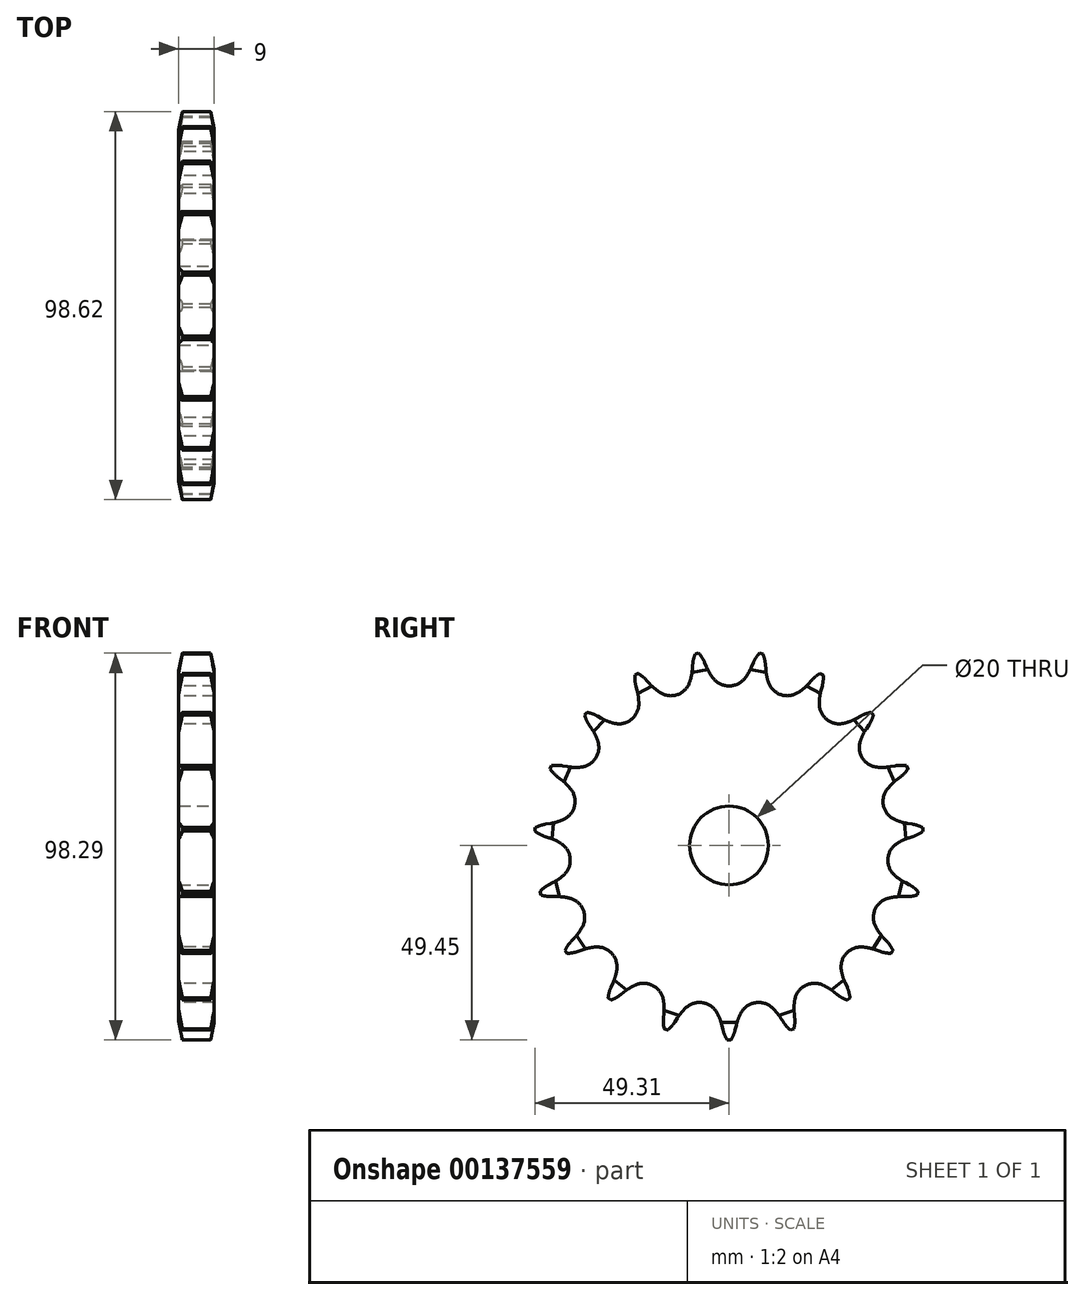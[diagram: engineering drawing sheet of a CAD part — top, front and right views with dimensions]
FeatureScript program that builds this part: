
annotation { "Feature Type Name" : "Feature", "Feature Type Description" : "" }
export const myFeature = defineFeature(function(context is Context, id is Id, definition is map)
    precondition{}
    {
        {
            assignVariable(context, id + "F0", {"name" : "P", "anyValue" : 15});
        }
        {
            assignVariable(context, id + "F1", {"name" : "N", "anyValue" : 19});
        }
        {
            assignVariable(context, id + "F2", {"name" : "J", "anyValue" : 0.3 * getVariable(context, 'P')});
        }
        {
            var Q0;
            Q0=qCreatedBy(makeId("Right.planeOp"),FACE);
            var sketch = newSketch(context, id + "F3", { "sketchPlane" : qUnion([Q0])});
            skCircle(sketch, "E0", {"center": v(0, 0) * mm, "radius": 45.57 * mm, "construction": true});
            skLineSegment(sketch, "E1", {"start": v(0, 45.57) * mm, "end": v(14.8, 43.1) * mm, "construction": true});
            skLineSegment(sketch, "E2", {"start": v(-5.72, 45.38) * mm, "end": v(6.3, 50.5) * mm, "construction": true});
            skLineSegment(sketch, "E3", {"start": v(6.3, 50.5) * mm, "end": v(-3.98, 42.44) * mm, "construction": true});
            skLineSegment(sketch, "E4", {"start": v(-15.64, 45.57) * mm, "end": v(15.64, 45.57) * mm, "construction": true});
            skLineSegment(sketch, "E5", {"start": v(0, 0) * mm, "end": v(0, 40.5) * mm});
            skLineSegment(sketch, "E6", {"start": v(0, 0) * mm, "end": v(-14.8, 43.1) * mm, "construction": true});
            skLineSegment(sketch, "E7", {"start": v(0, 0) * mm, "end": v(14.8, 43.1) * mm, "construction": true});
            skArc(sketch, "E8", {"start": v(-5.72, 45.38) * mm, "mid": v(-4.95, 43.85) * mm, "end": v(-3.98, 42.44) * mm});
            skLineSegment(sketch, "E9", {"start": v(-5.72, 45.38) * mm, "end": v(-6.2, 46.5) * mm});
            skLineSegment(sketch, "E10.trimOffspring", {"start": v(-14.8, 43.1) * mm, "end": v(0, 45.57) * mm, "construction": true});
            skLineSegment(sketch, "E11", {"start": v(-6.2, 46.5) * mm, "end": v(-13.8, 43.26) * mm, "construction": true});
            skLineSegment(sketch, "E12", {"start": v(-7.4, 44.33) * mm, "end": v(-8.24, 49.37) * mm, "construction": true});
            skArc(sketch, "E13", {"start": v(-6.2, 46.5) * mm, "mid": v(-6.86, 47.74) * mm, "end": v(-7.7, 48.84) * mm});
            skArc(sketch, "E14.trimOffspring", {"start": v(-3.98, 42.44) * mm, "mid": v(-2.21, 41.01) * mm, "end": v(0, 40.5) * mm});
            skArc(sketch, "E15.MirrorCS", {"start": v(-9.23, 46) * mm, "mid": v(-9.01, 47.38) * mm, "end": v(-8.57, 48.7) * mm});
            skLineSegment(sketch, "E16.MirrorCS", {"start": v(-9.32, 44.78) * mm, "end": v(-9.23, 46) * mm});
            skArc(sketch, "E17.MirrorCS", {"start": v(-9.32, 44.78) * mm, "mid": v(-9.56, 43.08) * mm, "end": v(-10.01, 41.43) * mm});
            skArc(sketch, "E18.MirrorCS", {"start": v(-10.01, 41.43) * mm, "mid": v(-11.22, 39.5) * mm, "end": v(-13.15, 38.3) * mm});
            skLineSegment(sketch, "E19.MirrorCS", {"start": v(0, 0) * mm, "end": v(-13.15, 38.3) * mm});
            skPoint(sketch, "E20.orphan", {"position": v(-8.24, 49.37) * mm});
            skLineSegment(sketch, "E21", {"start": v(-8.57, 48.7) * mm, "end": v(-7.7, 48.84) * mm});
            skCircle(sketch, "E22", {"center": v(0, 0) * mm, "radius": 10 * mm});
            skSolve(sketch);
        }
        {
            var Q0;
            Q0=makeQuery(id+"F3.imprint","IMPRINT",FACE,{"disambiguationData":[TD([[makeQuery(id+"F3.imprint","IMPRINT",EDGE,{"derivedFrom":sQuery(id+"F3.wireOp",EDGE,"E5")}),1.0]])]});
            var Q1;
            Q1=makeQuery(id+"F3.imprint","IMPRINT",FACE,{"disambiguationData":[TD([[makeQuery(id+"F3.imprint","IMPRINT",EDGE,{"derivedFrom":sQuery(id+"F3.wireOp",EDGE,"E8")}),-1.0]])]});
            extrude(context, id + "F4", {"entities" : qUnion([Q0, Q1]), "depth" : 9 * mm});
        }
        {
            var Q0;
            Q0=makeQuery(id+"F4.opExtrude","CAP_EDGE",EDGE,{"disambiguationData":[OSD([sQuery(id+"F3.wireOp",EDGE,"E21")])],"isStart":false});
            var Q1;
            Q1=makeQuery(id+"F4.opExtrude","CAP_EDGE",EDGE,{"disambiguationData":[OSD([sQuery(id+"F3.wireOp",EDGE,"E21")])],"isStart":true});
            chamfer(context, id + "F5", {"entities" : qUnion([Q0, Q1]), "chamferType" : ChamferType.TWO_OFFSETS, "width1" : (getVariable(context, 'J') / 5) * mm, "oppositeDirection" : false, "width2" : (getVariable(context, 'J')) * mm, "tangentPropagation" : true});
        }
        {
            var Q0;
            Q0=makeQuery(id+"F4.opExtrude","SWEPT_BODY",BODY,{"disambiguationData":[OSD([sQuery(id+"F3.wireOp",EDGE,"E5"),sQuery(id+"F3.wireOp",EDGE,"E8"),sQuery(id+"F3.wireOp",EDGE,"E9"),sQuery(id+"F3.wireOp",EDGE,"E13"),sQuery(id+"F3.wireOp",EDGE,"E14.trimOffspring"),sQuery(id+"F3.wireOp",EDGE,"E15.MirrorCS"),sQuery(id+"F3.wireOp",EDGE,"E16.MirrorCS"),sQuery(id+"F3.wireOp",EDGE,"E17.MirrorCS"),sQuery(id+"F3.wireOp",EDGE,"E18.MirrorCS"),sQuery(id+"F3.wireOp",EDGE,"E19.MirrorCS"),sQuery(id+"F3.wireOp",EDGE,"E21")])]});
            var Q1;
            Q1=makeQuery(id+"F4.opExtrude","SWEPT_EDGE",EDGE,{"disambiguationData":[OSD([sQuery(id+"F3.wireOp",EDGE,"E5"),sQuery(id+"F3.wireOp",EDGE,"E19.MirrorCS")])]});
            circularPattern(context, id + "F6", {"operationType" : NewBodyOperationType.ADD, "entities" : qUnion([Q0]), "axis" : qUnion([Q1]), "angle" : (360 / getVariable(context, 'N')) * degree, "instanceCount" : getVariable(context, 'N')});
        }
        {
            var Q0;
            {var subQ0=sQuery(id+"F3.wireOp",EDGE,"E19.MirrorCS");var subQ1=sQuery(id+"F3.wireOp",EDGE,"E5");var subQ2=makeQuery(id+"F3.imprint","INTERSECT",VERTEX,{"derivedFrom":[subQ1,subQ0]});Q0=makeQuery(id+"F3.imprint","IMPRINT",FACE,{"disambiguationData":[TD([[makeQuery(id+"F3.imprint","IMPRINT",EDGE,{"disambiguationData":[TD([[subQ2,-1.0]])],"derivedFrom":subQ1}),-1.0]])]});}
            var Q1;
            {var subQ0=sQuery(id+"F3.wireOp",EDGE,"E19.MirrorCS");var subQ1=sQuery(id+"F3.wireOp",EDGE,"E5");var subQ2=makeQuery(id+"F3.imprint","INTERSECT",VERTEX,{"derivedFrom":[subQ1,subQ0]});Q1=makeQuery(id+"F3.imprint","IMPRINT",FACE,{"disambiguationData":[TD([[makeQuery(id+"F3.imprint","IMPRINT",EDGE,{"disambiguationData":[TD([[subQ2,-1.0]])],"derivedFrom":subQ1}),1.0]])]});}
            var Q2;
            Q2=sQuery(id+"F3.wireOp",EDGE,"E22");
            extrude(context, id + "F7", {"entities" : qUnion([Q0, Q1]), "operationType" : NewBodyOperationType.REMOVE, "surfaceEntities" : qUnion([Q2]), "endBound" : BoundingType.SYMMETRIC, "oppositeDirection" : true, "depth" : 25 * mm});
        }
    });
